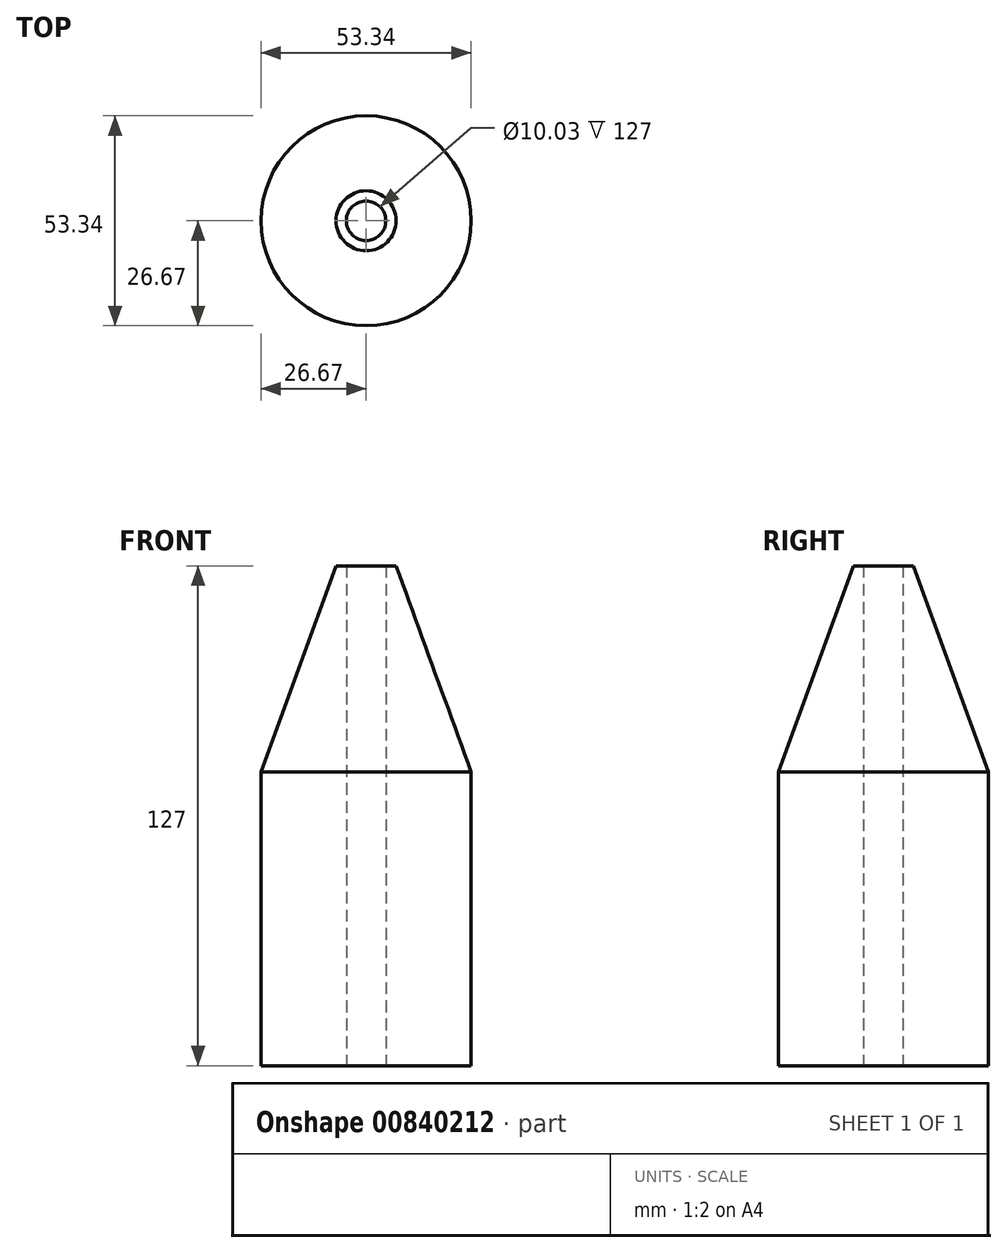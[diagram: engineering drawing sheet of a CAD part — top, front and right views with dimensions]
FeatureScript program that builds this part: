
annotation { "Feature Type Name" : "Feature", "Feature Type Description" : "" }
export const myFeature = defineFeature(function(context is Context, id is Id, definition is map)
    precondition{}
    {
        {
            var Q0;
            Q0=qCreatedBy(makeId("Top.planeOp"),FACE);
            var sketch = newSketch(context, id + "F0", { "sketchPlane" : qUnion([Q0])});
            skCircle(sketch, "E0", {"center": v(0, 0) * mm, "radius": 26.67 * mm});
            skSolve(sketch);
        }
        {
            var Q0;
            Q0=makeQuery(id+"F0.imprint","IMPRINT",FACE,{"disambiguationData":[TD([[makeQuery(id+"F0.imprint","IMPRINT",EDGE,{"derivedFrom":sQuery(id+"F0.wireOp",EDGE,"E0")}),1.0]])]});
            extrude(context, id + "F1", {"entities" : qUnion([Q0]), "depth" : 101.6 * mm, "offsetDistance" : 25.4 * mm});
        }
        {
            var Q0;
            Q0=makeQuery(id+"F1.opExtrude","CAP_EDGE",EDGE,{"disambiguationData":[OSD([sQuery(id+"F0.wireOp",EDGE,"E0")])],"isStart":false});
            chamfer(context, id + "F2", {"entities" : qUnion([Q0]), "chamferType" : ChamferType.OFFSET_ANGLE, "width" : 19.05 * mm, "oppositeDirection" : false, "angle" : 70 * degree, "tangentPropagation" : true});
        }
        {
            var Q0;
            Q0=makeQuery(id+"F1.opExtrude","CAP_FACE",FACE,{"disambiguationData":[OSD([sQuery(id+"F0.wireOp",EDGE,"E0")])],"isStart":true});
            var sketch = newSketch(context, id + "F3", { "sketchPlane" : qUnion([Q0])});
            skCircle(sketch, "E1", {"center": v(0, 0) * mm, "radius": 5.02 * mm});
            skSolve(sketch);
        }
        {
            var Q0;
            Q0=makeQuery(id+"F3.imprint","IMPRINT",FACE,{"disambiguationData":[TD([[makeQuery(id+"F3.imprint","IMPRINT",EDGE,{"derivedFrom":sQuery(id+"F3.wireOp",EDGE,"E1")}),1.0]])]});
            extrude(context, id + "F4", {"entities" : qUnion([Q0]), "operationType" : NewBodyOperationType.REMOVE, "oppositeDirection" : true, "depth" : 101.6 * mm, "offsetDistance" : 25.4 * mm});
        }
        {
            var Q0;
            Q0=makeQuery(id+"F1.opExtrude","CAP_FACE",FACE,{"disambiguationData":[OSD([sQuery(id+"F0.wireOp",EDGE,"E0")])],"isStart":true});
            extrude(context, id + "F5", {"entities" : qUnion([Q0]), "operationType" : NewBodyOperationType.ADD, "depth" : 25.4 * mm, "offsetDistance" : 25.4 * mm});
        }
    });
